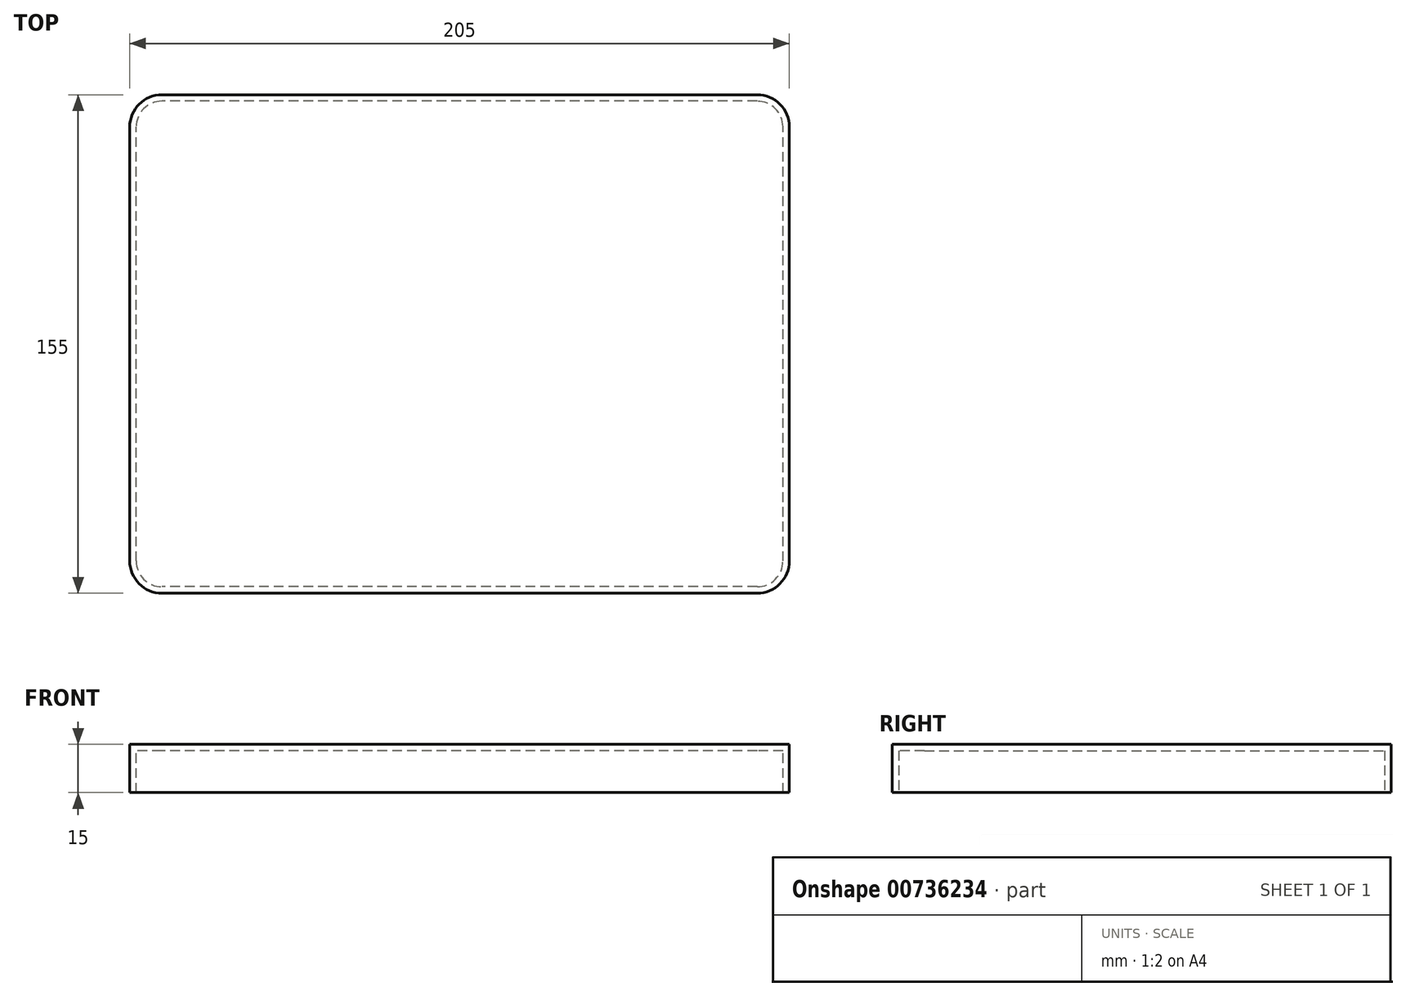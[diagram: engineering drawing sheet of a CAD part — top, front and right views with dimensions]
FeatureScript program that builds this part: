
annotation { "Feature Type Name" : "Feature", "Feature Type Description" : "" }
export const myFeature = defineFeature(function(context is Context, id is Id, definition is map)
    precondition{}
    {
        {
            var Q0;
            Q0=qCreatedBy(makeId("Top.planeOp"),FACE);
            var sketch = newSketch(context, id + "F0", { "sketchPlane" : qUnion([Q0])});
            skLineSegment(sketch, "E0.bottom", {"start": v(92.5, -77.5) * mm, "end": v(-92.5, -77.5) * mm});
            skLineSegment(sketch, "E0.top", {"start": v(92.5, 77.5) * mm, "end": v(-92.5, 77.5) * mm});
            skLineSegment(sketch, "E0.left", {"start": v(102.5, -67.5) * mm, "end": v(102.5, 67.5) * mm});
            skLineSegment(sketch, "E0.right", {"start": v(-102.5, -67.5) * mm, "end": v(-102.5, 67.5) * mm});
            skPoint(sketch, "E0.middle", {"position": v(0, 0) * mm});
            skPoint(sketch, "E1.visualSharp", {"position": v(-102.5, 77.5) * mm});
            skArc(sketch, "E1.filletArc", {"start": v(-92.5, 77.5) * mm, "mid": v(-99.57, 74.57) * mm, "end": v(-102.5, 67.5) * mm});
            skPoint(sketch, "E2.visualSharp", {"position": v(102.5, 77.5) * mm});
            skArc(sketch, "E2.filletArc", {"start": v(102.5, 67.5) * mm, "mid": v(99.57, 74.57) * mm, "end": v(92.5, 77.5) * mm});
            skPoint(sketch, "E3.visualSharp", {"position": v(102.5, -77.5) * mm});
            skArc(sketch, "E3.filletArc", {"start": v(92.5, -77.5) * mm, "mid": v(99.57, -74.57) * mm, "end": v(102.5, -67.5) * mm});
            skPoint(sketch, "E4.visualSharp", {"position": v(-102.5, -77.5) * mm});
            skArc(sketch, "E4.filletArc", {"start": v(-102.5, -67.5) * mm, "mid": v(-99.57, -74.57) * mm, "end": v(-92.5, -77.5) * mm});
            skSolve(sketch);
        }
        {
            var Q0;
            Q0=makeQuery(id+"F0.imprint","IMPRINT",FACE,{"disambiguationData":[TD([[makeQuery(id+"F0.imprint","IMPRINT",EDGE,{"derivedFrom":sQuery(id+"F0.wireOp",EDGE,"E0.bottom")}),-1.0]])]});
            extrude(context, id + "F1", {"entities" : qUnion([Q0]), "endBound" : BoundingType.SYMMETRIC, "depth" : 15 * mm, "offsetDistance" : 25 * mm});
        }
        {
            var Q0;
            Q0=makeQuery(id+"F1.opExtrude","CAP_FACE",FACE,{"disambiguationData":[OSD([sQuery(id+"F0.wireOp",EDGE,"E0.bottom"),sQuery(id+"F0.wireOp",EDGE,"E0.top"),sQuery(id+"F0.wireOp",EDGE,"E0.left"),sQuery(id+"F0.wireOp",EDGE,"E0.right"),sQuery(id+"F0.wireOp",EDGE,"E1.filletArc"),sQuery(id+"F0.wireOp",EDGE,"E2.filletArc"),sQuery(id+"F0.wireOp",EDGE,"E3.filletArc"),sQuery(id+"F0.wireOp",EDGE,"E4.filletArc")])],"isStart":true});
            shell(context, id + "F2", {"entities" : qUnion([Q0]), "thickness" : 2 * mm});
        }
    });
